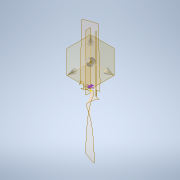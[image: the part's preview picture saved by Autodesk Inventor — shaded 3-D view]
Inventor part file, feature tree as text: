
AUTODESK INVENTOR PART (.ipt)
format: ipt  version: 2022 (Build 260153000, 153)  size: 4,939,776 bytes
history: native  units: mm
features: sketch x8, plane x3, mirror x2, boolean_combine x2, other x2, loft x1, sweep x1, extrude x1, surface_op x1
ambient origin geometry x8: Origin, YZ Plane, XZ Plane, XY Plane, X Axis, Y Axis, Z Axis, Center Point
bodies: Solid10 (feature_tree), Solid12 (feature_tree), Solid13 (feature_tree)
feature tree (21):
  sketch  "Sketch1"  dims[d3=30.0mm d27=20.0mm]
  sketch  "Sketch2"  dims[d33=7.5mm d34=2.0mm]
  plane  "Work Plane1"
  sketch  "3D Sketch1"
  sketch  "Sketch4"  dims[d35=0.0mm d36=90.0deg d37=0.0mm d38=90.0deg]
  plane  "Work Plane2"
  sketch  "Sketch6"  dims[d39=-7.5mm]
  loft  "Loft1"
  plane  "Work Plane3"
  sweep  "Sweep13"
  mirror  "Mirror3"
  mirror  "Mirror4"
  sketch  "Sketch8"  dims[d43=7.5mm d44=310.0mm d45=0.0mm d46=0.0mm d47=680.0mm d48=90.0deg d49=50.0mm d51=70.0mm d52=0.0mm d53=0.0mm d50=0.5mm d54=0.872665mm]
  boolean_combine  "Combine1"
  extrude  "Extrusion2"  TaperAngle=0.0deg  [1 undecoded]
  boolean_combine  "Combine2"
  sketch  "Sketch7"  dims[d42=20.0mm]
  other  "Pattern of Solid10:2"
  sketch  "3D Sketch2"
  other  "Srf1"
  surface_op  "Boundary Patch1"
note: 1 required parameter value undecoded (feature->parameter linkage not recoverable at this tier; creation-order binding heuristic only, values carry confidence <= 0.55)
